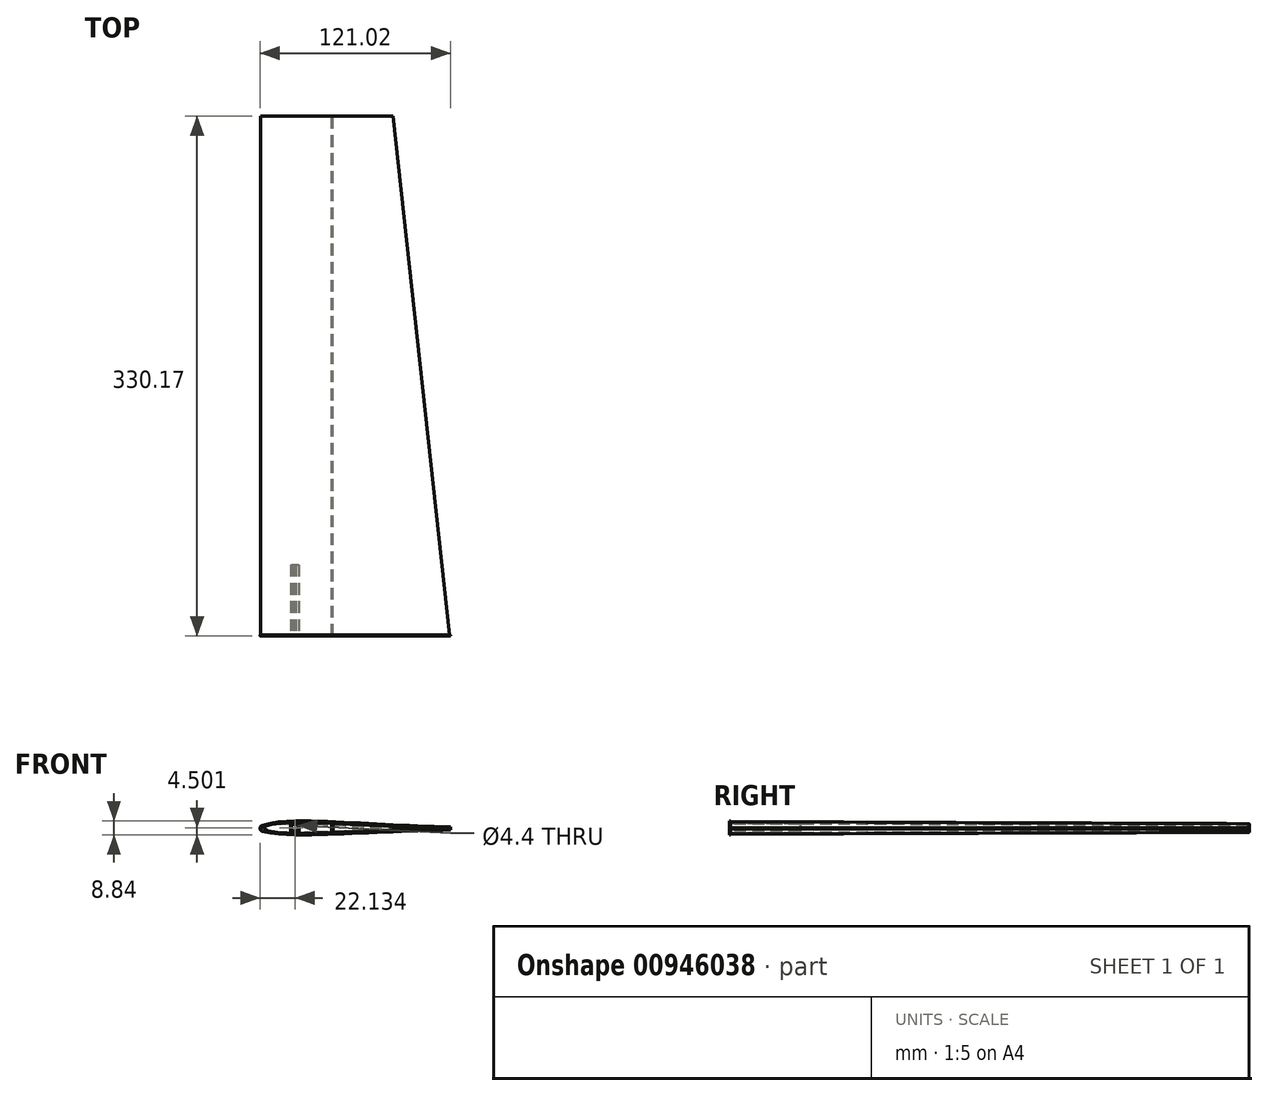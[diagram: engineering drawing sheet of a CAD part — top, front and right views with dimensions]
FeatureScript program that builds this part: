
annotation { "Feature Type Name" : "Feature", "Feature Type Description" : "" }
export const myFeature = defineFeature(function(context is Context, id is Id, definition is map)
    precondition{}
    {
        {
            var Q0;
            Q0=qCreatedBy(makeId("Front.planeOp"),FACE);
            var sketch = newSketch(context, id + "F0", { "sketchPlane" : qUnion([Q0])});
            skPoint(sketch, "E0.middle", {"position": v(0, 0) * mm});
            skPoint(sketch, "E1", {"position": v(-20, 4) * mm});
            skPoint(sketch, "E2", {"position": v(-20, -4) * mm});
            skPoint(sketch, "E3", {"position": v(-63.38, 0) * mm});
            skPoint(sketch, "E4", {"position": v(-38.15, 4.26) * mm});
            skPoint(sketch, "E5", {"position": v(-38.15, -3.52) * mm});
            skArc(sketch, "E6", {"start": v(-58.92, 1.48) * mm, "mid": v(-60, 0.01) * mm, "end": v(-58.88, -1.42) * mm});
            skPoint(sketch, "E6.centerSnap0", {"position": v(-60, 0.03) * mm});
            skPoint(sketch, "E7.orphan", {"position": v(-60, 4.03) * mm});
            skPoint(sketch, "E8.orphan", {"position": v(-60.01, -3.97) * mm});
            skPoint(sketch, "E9.orphan", {"position": v(60.01, 3.97) * mm});
            skPoint(sketch, "E10.orphan", {"position": v(60, -4.03) * mm});
            skLineSegment(sketch, "E11", {"start": v(60, -0.03) * mm, "end": v(60, 0.47) * mm});
            skLineSegment(sketch, "E12", {"start": v(60, -0.03) * mm, "end": v(60, -0.53) * mm});
            skFitSpline(sketch, "E13", {"points": [v(-58.88, -1.42) * mm, v(-38.15, -3.52) * mm, v(60, -0.53) * mm], "startDerivative": vector(51.85, -10.71) * mm, "endDerivative": vector(168.15, 2.34) * mm});
            skFitSpline(sketch, "E14", {"points": [v(-58.92, 1.48) * mm, v(-38.15, 4.26) * mm, v(60, 0.47) * mm], "startDerivative": vector(55.26, 16.33) * mm, "endDerivative": vector(170.94, -3.98) * mm});
            skSolve(sketch);
        }
        {
            var Q0;
            Q0=makeQuery(id+"F0.imprint","IMPRINT",FACE,{"disambiguationData":[TD([[makeQuery(id+"F0.imprint","IMPRINT",EDGE,{"derivedFrom":sQuery(id+"F0.wireOp",EDGE,"c9sgiWDQ-z4xn-Ypo2-fUFO-b6gQvCFeg78z")}),-1.0]])]});
            var Q1;
            Q1=makeQuery(id+"F0.imprint","IMPRINT",FACE,{"disambiguationData":[TD([[makeQuery(id+"F0.imprint","IMPRINT",EDGE,{"derivedFrom":sQuery(id+"F0.wireOp",EDGE,"E6")}),1.0]])]});
            extrude(context, id + "F1", {"entities" : qUnion([Q0, Q1]), "endBound" : BoundingType.SYMMETRIC, "depth" : 0.2 * mm, "offsetDistance" : 25 * mm});
        }
        {
            var Q0;
            Q0=makeQuery(id+"F1.opExtrude","SWEPT_BODY",BODY,{"disambiguationData":[OSD([sQuery(id+"F0.wireOp",EDGE,"E6"),sQuery(id+"F0.wireOp",EDGE,"E11"),sQuery(id+"F0.wireOp",EDGE,"E12"),sQuery(id+"F0.wireOp",EDGE,"E13"),sQuery(id+"F0.wireOp",EDGE,"E14")])]});
            var Q1;
            Q1=sQuery(id+"F0.wireOp",VERTEX,"E6.centerSnap0");
            transform(context, id + "F2", {"entities" : qUnion([Q0]), "transformType" : TransformType.SCALE_UNIFORMLY, "scale" : 0.7, "scalePoint" : qUnion([Q1]), "makeCopy" : true});
        }
        {
            var Q0;
            Q0=makeQuery(id+"F2.opPattern","COPY",BODY,{"derivedFrom":makeQuery(id+"F1.opExtrude","SWEPT_BODY",BODY,{"disambiguationData":[OSD([sQuery(id+"F0.wireOp",EDGE,"E6"),sQuery(id+"F0.wireOp",EDGE,"E11"),sQuery(id+"F0.wireOp",EDGE,"E12"),sQuery(id+"F0.wireOp",EDGE,"E13"),sQuery(id+"F0.wireOp",EDGE,"E14")])]}),"instanceName":"1"});
            transform(context, id + "F3", {"entities" : qUnion([Q0]), "transformType" : TransformType.TRANSLATION_3D, "dx" : 0 * mm, "dy" : 330 * mm, "dz" : 0 * mm, "makeCopy" : false});
        }
        {
            var Q0;
            Q0=makeQuery(id+"F1.opExtrude","CAP_FACE",FACE,{"disambiguationData":[OSD([sQuery(id+"F0.wireOp",EDGE,"E6"),sQuery(id+"F0.wireOp",EDGE,"E11"),sQuery(id+"F0.wireOp",EDGE,"E12"),sQuery(id+"F0.wireOp",EDGE,"E13"),sQuery(id+"F0.wireOp",EDGE,"E14")])],"isStart":true});
            var Q1;
            Q1=makeQuery(id+"F2.opPattern","COPY",FACE,{"derivedFrom":makeQuery(id+"F1.opExtrude","CAP_FACE",FACE,{"disambiguationData":[OSD([sQuery(id+"F0.wireOp",EDGE,"E6"),sQuery(id+"F0.wireOp",EDGE,"E11"),sQuery(id+"F0.wireOp",EDGE,"E12"),sQuery(id+"F0.wireOp",EDGE,"E13"),sQuery(id+"F0.wireOp",EDGE,"E14")])],"isStart":false}),"instanceName":"1"});
            loft(context, id + "F4", {"sheetProfilesArray" : [{ "sheetProfileEntities" : qUnion([Q0]) }, { "sheetProfileEntities" : qUnion([Q1]) }]});
        }
        {
            var Q0;
            Q0=makeQuery(id+"F1.opExtrude","CAP_FACE",FACE,{"disambiguationData":[OSD([sQuery(id+"F0.wireOp",EDGE,"E6"),sQuery(id+"F0.wireOp",EDGE,"E11"),sQuery(id+"F0.wireOp",EDGE,"E12"),sQuery(id+"F0.wireOp",EDGE,"E13"),sQuery(id+"F0.wireOp",EDGE,"E14")])],"isStart":false});
            shell(context, id + "F5", {"entities" : qUnion([Q0]), "thickness" : 0.5 * mm, "oppositeDirection" : true});
        }
        {
            var Q0;
            {var subQ0=sQuery(id+"F0.wireOp",EDGE,"E14");var subQ1=sQuery(id+"F0.wireOp",EDGE,"E13");var subQ2=sQuery(id+"F0.wireOp",EDGE,"E12");var subQ3=sQuery(id+"F0.wireOp",EDGE,"E11");var subQ4=sQuery(id+"F0.wireOp",EDGE,"E6");Q0=makeQuery(id+"F4.opLoft","CAP_FACE",FACE,{"disambiguationData":[OSD([subQ4,subQ3,subQ2,subQ1,subQ0]),TDD([makeQuery(id+"F1.opExtrude","CAP_FACE",FACE,{"disambiguationData":[OSD([subQ4,subQ3,subQ2,subQ1,subQ0])],"isStart":true})])],"isStart":true});}
            shell(context, id + "F6", {"entities" : qUnion([Q0]), "thickness" : 0.5 * mm});
        }
        {
            var Q0;
            Q0=qCreatedBy(makeId("Front.planeOp"),FACE);
            var sketch = newSketch(context, id + "F7", { "sketchPlane" : qUnion([Q0])});
            skPoint(sketch, "E15.middle", {"position": v(0, 0) * mm});
            skPoint(sketch, "E16", {"position": v(-20, 4) * mm});
            skPoint(sketch, "E17", {"position": v(-20, -4) * mm});
            skPoint(sketch, "E18", {"position": v(-63.39, 0) * mm});
            skPoint(sketch, "E19", {"position": v(-38.16, 4.26) * mm});
            skPoint(sketch, "E20", {"position": v(-38.16, -3.53) * mm});
            skArc(sketch, "E21", {"start": v(-58.93, 1.47) * mm, "mid": v(-60.02, 0) * mm, "end": v(-58.9, -1.42) * mm});
            skPoint(sketch, "E21.centerSnap0", {"position": v(-60.02, 0.03) * mm});
            skPoint(sketch, "E22.orphan", {"position": v(-60.01, 4.03) * mm});
            skPoint(sketch, "E23.orphan", {"position": v(-60.02, -3.97) * mm});
            skPoint(sketch, "E24.orphan", {"position": v(60, 3.96) * mm});
            skPoint(sketch, "E25.orphan", {"position": v(60, -4.04) * mm});
            skCircle(sketch, "E26", {"center": v(-38.38, 0.45) * mm, "radius": 2.2 * mm});
            skLineSegment(sketch, "E27", {"start": v(-35.59, 3.78) * mm, "end": v(-35.59, -3) * mm});
            skLineSegment(sketch, "E28", {"start": v(-41.26, -2.88) * mm, "end": v(-41.25, 3.7) * mm});
            skLineSegment(sketch, "E29", {"start": v(8.56, 2.1) * mm, "end": v(8.56, -1.65) * mm});
            skLineSegment(sketch, "E30", {"start": v(9.67, 2.05) * mm, "end": v(9.67, -1.6) * mm});
            skLineSegment(sketch, "E31", {"start": v(60, -0.04) * mm, "end": v(60, 0.46) * mm});
            skLineSegment(sketch, "E32", {"start": v(60, -0.04) * mm, "end": v(60, -0.54) * mm});
            skFitSpline(sketch, "E33", {"points": [v(-58.9, -1.42) * mm, v(-38.16, -3.53) * mm, v(60, -0.54) * mm], "startDerivative": vector(51.85, -10.71) * mm, "endDerivative": vector(168.15, 2.34) * mm});
            skFitSpline(sketch, "E34", {"points": [v(-58.93, 1.47) * mm, v(-38.16, 4.26) * mm, v(60, 0.46) * mm], "startDerivative": vector(55.26, 16.33) * mm, "endDerivative": vector(170.94, -3.98) * mm});
            skLineSegment(sketch, "E35", {"start": v(-41.25, 3.7) * mm, "end": v(-38.6, 3.73) * mm});
            skLineSegment(sketch, "E36", {"start": v(-38.6, 3.73) * mm, "end": v(-37.68, 3.78) * mm});
            skLineSegment(sketch, "E37", {"start": v(-37.68, 3.78) * mm, "end": v(-35.59, 3.78) * mm});
            skLineSegment(sketch, "E38", {"start": v(-41.26, -2.88) * mm, "end": v(-39.27, -3) * mm});
            skLineSegment(sketch, "E39", {"start": v(-39.27, -3) * mm, "end": v(-35.59, -3) * mm});
            skLineSegment(sketch, "E40", {"start": v(8.56, -1.65) * mm, "end": v(9.67, -1.6) * mm});
            skLineSegment(sketch, "E41", {"start": v(8.56, 2.1) * mm, "end": v(9.67, 2.05) * mm});
            skSolve(sketch);
        }
        {
            var Q0;
            Q0=makeQuery(id+"F7.imprint","IMPRINT",FACE,{"disambiguationData":[TD([[makeQuery(id+"F7.imprint","IMPRINT",EDGE,{"derivedFrom":sQuery(id+"F7.wireOp",EDGE,"E26")}),-1.0]])]});
            extrude(context, id + "F8", {"entities" : qUnion([Q0]), "oppositeDirection" : true, "depth" : 45 * mm, "offsetDistance" : 25 * mm});
        }
        {
            var Q0;
            Q0=qCreatedBy(makeId("Right.planeOp"),FACE);
            cPlane(context, id + "F9", {"entities" : qUnion([Q0]), "cplaneType" : CPlaneType.OFFSET, "offset" : 15 * mm, "oppositeDirection" : true, "width" : 150 * mm, "height" : 150 * mm});
        }
        {
            var Q0;
            Q0=qCreatedBy(id+"F9.planeOp",FACE);
            var sketch = newSketch(context, id + "F10", { "sketchPlane" : qUnion([Q0])});
            skLineSegment(sketch, "E42", {"start": v(0, 0) * mm, "end": v(0, -2.56) * mm});
            skLineSegment(sketch, "E43", {"start": v(0, -2.56) * mm, "end": v(0, 3.18) * mm});
            skLineSegment(sketch, "E44", {"start": v(0, -2.56) * mm, "end": v(329.97, -1.28) * mm});
            skPoint(sketch, "E44.endSnap0", {"position": v(0, -1.28) * mm});
            skLineSegment(sketch, "E45", {"start": v(0, 3.18) * mm, "end": v(330.01, 1.83) * mm});
            skLineSegment(sketch, "E46", {"start": v(330.01, 1.83) * mm, "end": v(329.97, -1.28) * mm});
            skSolve(sketch);
        }
        {
            var Q0;
            Q0=makeQuery(id+"F2.opPattern","COPY",FACE,{"derivedFrom":makeQuery(id+"F1.opExtrude","CAP_FACE",FACE,{"disambiguationData":[OSD([sQuery(id+"F0.wireOp",EDGE,"E6"),sQuery(id+"F0.wireOp",EDGE,"E11"),sQuery(id+"F0.wireOp",EDGE,"E12"),sQuery(id+"F0.wireOp",EDGE,"E13"),sQuery(id+"F0.wireOp",EDGE,"E14")])],"isStart":true}),"instanceName":"1"});
            cPlane(context, id + "F11", {"entities" : qUnion([Q0]), "cplaneType" : CPlaneType.OFFSET, "offset" : 0 * mm, "width" : 150 * mm, "height" : 150 * mm});
        }
        {
            var Q0;
            {var subQ0=sQuery(id+"F10.wireOp",EDGE,"E44");Q0=makeQuery(id+"F10.imprint","IMPRINT",FACE,{"disambiguationData":[TD([[makeQuery(id+"F10.imprint","IMPRINT",EDGE,{"derivedFrom":subQ0}),1.0]])]});}
            extrude(context, id + "F12", {"entities" : qUnion([Q0]), "depth" : 1 * mm, "offsetDistance" : 25 * mm});
        }
    });
